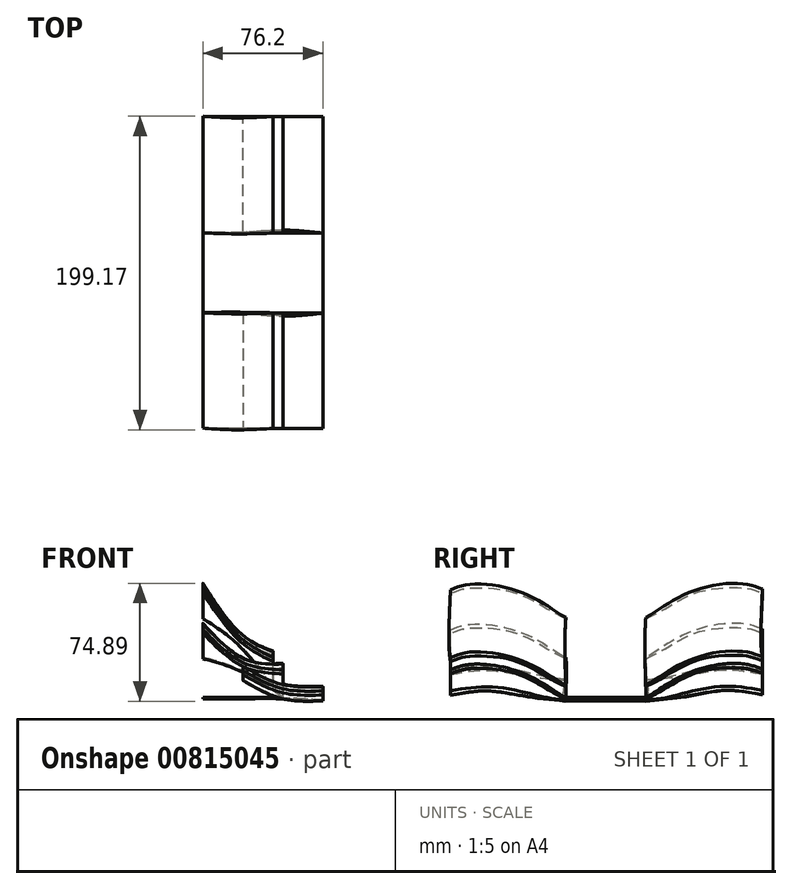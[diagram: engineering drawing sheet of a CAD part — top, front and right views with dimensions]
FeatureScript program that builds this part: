
annotation { "Feature Type Name" : "Feature", "Feature Type Description" : "" }
export const myFeature = defineFeature(function(context is Context, id is Id, definition is map)
    precondition{}
    {
        {
            var Q0;
            Q0=qCreatedBy(makeId("Right.planeOp"),FACE);
            cPlane(context, id + "F0", {"entities" : qUnion([Q0]), "cplaneType" : CPlaneType.OFFSET, "offset" : 25.4 * mm, "width" : 152.4 * mm, "height" : 152.4 * mm});
        }
        {
            var Q0;
            Q0=qCreatedBy(makeId("Right.planeOp"),FACE);
            cPlane(context, id + "F1", {"entities" : qUnion([Q0]), "cplaneType" : CPlaneType.OFFSET, "offset" : 25.4 * mm, "oppositeDirection" : true, "width" : 152.4 * mm, "height" : 152.4 * mm});
        }
        {
            var Q0;
            Q0=qCreatedBy(makeId("Right.planeOp"),FACE);
            cPlane(context, id + "F2", {"entities" : qUnion([Q0]), "cplaneType" : CPlaneType.OFFSET, "offset" : 50.8 * mm, "oppositeDirection" : true, "width" : 152.4 * mm, "height" : 152.4 * mm});
        }
        {
            var Q0;
            Q0=qCreatedBy(makeId("Right.planeOp"),FACE);
            cPlane(context, id + "F3", {"entities" : qUnion([Q0]), "cplaneType" : CPlaneType.OFFSET, "offset" : 6.35 * mm, "oppositeDirection" : true, "width" : 152.4 * mm, "height" : 152.4 * mm});
        }
        {
            var Q0;
            Q0=qCreatedBy(makeId("Right.planeOp"),FACE);
            var sketch = newSketch(context, id + "F4", { "sketchPlane" : qUnion([Q0])});
            skLineSegment(sketch, "E0", {"start": v(-25.85, 6.27) * mm, "end": v(24.95, 6.27) * mm});
            skFitSpline(sketch, "E1", {"points": [v(99.07, 10.46) * mm, v(73.66, 13) * mm, v(48.26, 8.81) * mm, v(24.95, 6.27) * mm], "startDerivative": vector(-112.97, 16.95) * mm, "endDerivative": vector(-94.23, -11.78) * mm});
            skFitSpline(sketch, "E2", {"points": [v(-99.06, 10.06) * mm, v(-73.66, 12.6) * mm, v(-48.26, 8.81) * mm, v(-25.85, 6.27) * mm], "startDerivative": vector(112.13, 16.82) * mm, "endDerivative": vector(95.43, -11.93) * mm});
            skFitSpline(sketch, "E3", {"points": [v(-25.85, 7.04) * mm, v(-45.21, 10.06) * mm, v(-72.39, 15.14) * mm, v(-99.06, 12.6) * mm], "startDerivative": vector(-84.02, 3.38) * mm, "endDerivative": vector(-76.8, -13.35) * mm});
            skFitSpline(sketch, "E4", {"points": [v(24.95, 7.04) * mm, v(45.21, 10.08) * mm, v(72.4, 15.54) * mm, v(99.06, 13) * mm], "startDerivative": vector(91.6, 3.53) * mm, "endDerivative": vector(77.34, -13.44) * mm});
            skLineSegment(sketch, "E5", {"start": v(-25.85, 7.04) * mm, "end": v(24.95, 7.04) * mm});
            skLineSegment(sketch, "E6", {"start": v(-99.06, 12.6) * mm, "end": v(-99.06, 10.06) * mm});
            skLineSegment(sketch, "E7", {"start": v(99.06, 10.46) * mm, "end": v(99.06, 13) * mm});
            skLineSegment(sketch, "E8", {"start": v(-25.85, 7.04) * mm, "end": v(-25.85, 6.27) * mm});
            skLineSegment(sketch, "E9", {"start": v(24.95, 6.27) * mm, "end": v(24.95, 7.04) * mm});
            skFitSpline(sketch, "E10", {"points": [v(-25.85, 6.27) * mm, v(-43.98, 16.13) * mm, v(-63.82, 24.03) * mm, v(-88.57, 25.3) * mm, v(-99.06, 22.13) * mm], "startDerivative": vector(-69.96, 28.98) * mm, "endDerivative": vector(-79.54, -30.53) * mm});
            skLineSegment(sketch, "E11", {"start": v(-99.06, 22.13) * mm, "end": v(-99.06, 24.67) * mm});
            skFitSpline(sketch, "E12", {"points": [v(-99.06, 24.67) * mm, v(-88.75, 27.84) * mm, v(-66.16, 26.57) * mm, v(-42.63, 17.53) * mm, v(-25.85, 7.04) * mm], "startDerivative": vector(50.78, 20.31) * mm, "endDerivative": vector(71.67, -41.09) * mm});
            skFitSpline(sketch, "E13", {"points": [v(24.95, 6.27) * mm, v(43.1, 16.13) * mm, v(62.93, 24.43) * mm, v(88.57, 25.7) * mm, v(99.06, 22.52) * mm], "startDerivative": vector(70.38, 29.15) * mm, "endDerivative": vector(80.02, -30.71) * mm});
            skLineSegment(sketch, "E14", {"start": v(99.06, 22.52) * mm, "end": v(99.06, 25.06) * mm});
            skFitSpline(sketch, "E15", {"points": [v(99.06, 25.06) * mm, v(88.75, 28.24) * mm, v(65.26, 26.97) * mm, v(41.74, 17.53) * mm, v(24.95, 7.04) * mm], "startDerivative": vector(-51.09, 20.43) * mm, "endDerivative": vector(-72.11, -41.34) * mm});
            skSolve(sketch);
        }
        {
            var Q0;
            Q0=qCreatedBy(id+"F1.planeOp",FACE);
            var sketch = newSketch(context, id + "F5", { "sketchPlane" : qUnion([Q0])});
            skFitSpline(sketch, "E16", {"points": [v(99.06, 21.77) * mm, v(73.66, 24.3) * mm, v(48.26, 20.48) * mm, v(25.4, 17.94) * mm], "startDerivative": vector(-112.5, 16.87) * mm, "endDerivative": vector(-94.8, -11.84) * mm});
            skFitSpline(sketch, "E17", {"points": [v(-99.06, 21.76) * mm, v(-73.66, 24.3) * mm, v(-48.26, 20.48) * mm, v(-25.4, 17.94) * mm], "startDerivative": vector(112.48, 16.87) * mm, "endDerivative": vector(94.8, -11.85) * mm});
            skFitSpline(sketch, "E18", {"points": [v(-25.4, 18.7) * mm, v(-45.21, 21.76) * mm, v(-72.39, 26.84) * mm, v(-99.06, 24.3) * mm], "startDerivative": vector(-87.77, 3.58) * mm, "endDerivative": vector(-77.05, -13.4) * mm});
            skFitSpline(sketch, "E19", {"points": [v(25.4, 18.7) * mm, v(45.21, 21.75) * mm, v(72.4, 26.85) * mm, v(99.06, 24.3) * mm], "startDerivative": vector(87.85, 3.55) * mm, "endDerivative": vector(77.06, -13.4) * mm});
            skLineSegment(sketch, "E20", {"start": v(-99.06, 24.3) * mm, "end": v(-99.06, 21.76) * mm});
            skLineSegment(sketch, "E21", {"start": v(99.06, 21.77) * mm, "end": v(99.06, 24.3) * mm});
            skLineSegment(sketch, "E22", {"start": v(-25.4, 18.7) * mm, "end": v(-25.4, 17.94) * mm});
            skLineSegment(sketch, "E23", {"start": v(25.4, 18.7) * mm, "end": v(25.4, 17.94) * mm});
            skFitSpline(sketch, "E24", {"points": [v(99.06, 26.85) * mm, v(73.66, 29.4) * mm, v(48.26, 25.57) * mm, v(25.4, 23.03) * mm], "startDerivative": vector(-112.5, 16.87) * mm, "endDerivative": vector(-94.79, -11.84) * mm});
            skFitSpline(sketch, "E25", {"points": [v(-99.06, 26.85) * mm, v(-73.66, 29.39) * mm, v(-48.26, 25.57) * mm, v(-25.4, 23.03) * mm], "startDerivative": vector(112.48, 16.87) * mm, "endDerivative": vector(94.8, -11.85) * mm});
            skFitSpline(sketch, "E26", {"points": [v(-25.4, 23.8) * mm, v(-45.21, 26.85) * mm, v(-72.4, 31.93) * mm, v(-99.06, 29.39) * mm], "startDerivative": vector(-87.8, 3.58) * mm, "endDerivative": vector(-77.05, -13.4) * mm});
            skFitSpline(sketch, "E27", {"points": [v(25.4, 23.8) * mm, v(45.21, 26.84) * mm, v(72.4, 31.93) * mm, v(99.06, 29.4) * mm], "startDerivative": vector(87.89, 3.55) * mm, "endDerivative": vector(77.06, -13.4) * mm});
            skLineSegment(sketch, "E28", {"start": v(-99.06, 29.39) * mm, "end": v(-99.06, 26.85) * mm});
            skLineSegment(sketch, "E29", {"start": v(99.06, 26.85) * mm, "end": v(99.06, 29.4) * mm});
            skLineSegment(sketch, "E30", {"start": v(-25.4, 23.8) * mm, "end": v(-25.4, 23.03) * mm});
            skLineSegment(sketch, "E31", {"start": v(25.4, 23.8) * mm, "end": v(25.4, 23.03) * mm});
            skLineSegment(sketch, "E32.bottom", {"start": v(-25.4, 7.09) * mm, "end": v(25.4, 7.09) * mm});
            skLineSegment(sketch, "E32.top", {"start": v(-25.4, 6.32) * mm, "end": v(25.4, 6.32) * mm});
            skLineSegment(sketch, "E32.left", {"start": v(-25.4, 7.09) * mm, "end": v(-25.4, 6.32) * mm});
            skLineSegment(sketch, "E32.right", {"start": v(25.4, 7.09) * mm, "end": v(25.4, 6.32) * mm});
            skSolve(sketch);
        }
        {
            var Q0;
            Q0=qCreatedBy(id+"F0.planeOp",FACE);
            var sketch = newSketch(context, id + "F6", { "sketchPlane" : qUnion([Q0])});
            skLineSegment(sketch, "E33", {"start": v(-25.86, 4.98) * mm, "end": v(24.94, 4.98) * mm});
            skFitSpline(sketch, "E34", {"points": [v(99.06, 9.1) * mm, v(73.66, 11.65) * mm, v(48.26, 7.52) * mm, v(24.94, 4.98) * mm], "startDerivative": vector(-112.88, 16.93) * mm, "endDerivative": vector(-94.2, -11.77) * mm});
            skFitSpline(sketch, "E35", {"points": [v(-99.06, 8.76) * mm, v(-73.66, 11.3) * mm, v(-48.26, 7.52) * mm, v(-25.86, 4.98) * mm], "startDerivative": vector(112.12, 16.82) * mm, "endDerivative": vector(95.45, -11.93) * mm});
            skFitSpline(sketch, "E36", {"points": [v(-25.86, 5.74) * mm, v(-45.21, 8.76) * mm, v(-72.4, 13.84) * mm, v(-99.06, 11.3) * mm], "startDerivative": vector(-83.87, 3.27) * mm, "endDerivative": vector(-76.78, -13.34) * mm});
            skFitSpline(sketch, "E37", {"points": [v(24.94, 5.74) * mm, v(45.21, 8.79) * mm, v(72.4, 14.19) * mm, v(99.06, 11.65) * mm], "startDerivative": vector(91.74, 3.53) * mm, "endDerivative": vector(77.34, -13.44) * mm});
            skLineSegment(sketch, "E38", {"start": v(-25.86, 5.74) * mm, "end": v(24.94, 5.74) * mm});
            skLineSegment(sketch, "E39", {"start": v(-99.06, 11.3) * mm, "end": v(-99.06, 8.76) * mm});
            skLineSegment(sketch, "E40", {"start": v(99.06, 9.1) * mm, "end": v(99.06, 11.65) * mm});
            skLineSegment(sketch, "E41", {"start": v(-25.86, 5.74) * mm, "end": v(-25.86, 4.98) * mm});
            skLineSegment(sketch, "E42", {"start": v(24.94, 4.98) * mm, "end": v(24.94, 5.74) * mm});
            skSolve(sketch);
        }
        {
            var Q0;
            Q0=qCreatedBy(id+"F2.planeOp",FACE);
            var sketch = newSketch(context, id + "F7", { "sketchPlane" : qUnion([Q0])});
            skLineSegment(sketch, "E43", {"start": v(-25.76, 32.51) * mm, "end": v(-25.76, 31.75) * mm});
            skLineSegment(sketch, "E44", {"start": v(25.04, 31.75) * mm, "end": v(25.04, 32.51) * mm});
            skFitSpline(sketch, "E45", {"points": [v(-25.76, 31.75) * mm, v(-43.9, 41.6) * mm, v(-63.73, 49.51) * mm, v(-88.49, 50.78) * mm, v(-98.98, 47.6) * mm], "startDerivative": vector(-69.96, 28.98) * mm, "endDerivative": vector(-79.54, -30.53) * mm});
            skLineSegment(sketch, "E46", {"start": v(-98.98, 47.6) * mm, "end": v(-98.98, 50.15) * mm});
            skFitSpline(sketch, "E47", {"points": [v(-98.98, 50.15) * mm, v(-88.66, 53.32) * mm, v(-66.07, 52.05) * mm, v(-42.55, 43) * mm, v(-25.76, 32.51) * mm], "startDerivative": vector(50.78, 20.31) * mm, "endDerivative": vector(71.67, -41.09) * mm});
            skFitSpline(sketch, "E48", {"points": [v(25.04, 31.75) * mm, v(43.17, 41.6) * mm, v(63.01, 49.9) * mm, v(88.65, 51.17) * mm, v(99.14, 48) * mm], "startDerivative": vector(70.38, 29.15) * mm, "endDerivative": vector(80.02, -30.71) * mm});
            skLineSegment(sketch, "E49", {"start": v(99.14, 48) * mm, "end": v(99.14, 50.54) * mm});
            skFitSpline(sketch, "E50", {"points": [v(99.14, 50.54) * mm, v(88.83, 53.71) * mm, v(65.35, 52.44) * mm, v(41.83, 43) * mm, v(25.04, 32.51) * mm], "startDerivative": vector(-51.09, 20.43) * mm, "endDerivative": vector(-72.11, -41.34) * mm});
            skLineSegment(sketch, "E51", {"start": v(-25.73, 57.91) * mm, "end": v(-25.73, 57.15) * mm});
            skLineSegment(sketch, "E52", {"start": v(25.07, 57.15) * mm, "end": v(25.07, 57.91) * mm});
            skFitSpline(sketch, "E53", {"points": [v(-25.73, 57.15) * mm, v(-43.87, 67) * mm, v(-63.7, 74.91) * mm, v(-88.46, 76.18) * mm, v(-98.95, 73) * mm], "startDerivative": vector(-69.96, 28.98) * mm, "endDerivative": vector(-79.54, -30.53) * mm});
            skLineSegment(sketch, "E54", {"start": v(-98.95, 73) * mm, "end": v(-98.95, 75.55) * mm});
            skFitSpline(sketch, "E55", {"points": [v(-98.95, 75.55) * mm, v(-88.64, 78.72) * mm, v(-66.04, 77.45) * mm, v(-42.52, 68.4) * mm, v(-25.73, 57.91) * mm], "startDerivative": vector(50.78, 20.31) * mm, "endDerivative": vector(71.67, -41.09) * mm});
            skFitSpline(sketch, "E56", {"points": [v(25.07, 57.15) * mm, v(43.2, 67) * mm, v(63.04, 75.3) * mm, v(88.68, 76.57) * mm, v(99.17, 73.4) * mm], "startDerivative": vector(70.38, 29.15) * mm, "endDerivative": vector(80.02, -30.71) * mm});
            skLineSegment(sketch, "E57", {"start": v(99.17, 73.4) * mm, "end": v(99.17, 75.94) * mm});
            skFitSpline(sketch, "E58", {"points": [v(99.17, 75.94) * mm, v(88.86, 79.11) * mm, v(65.38, 77.84) * mm, v(41.86, 68.4) * mm, v(25.07, 57.91) * mm], "startDerivative": vector(-51.09, 20.43) * mm, "endDerivative": vector(-72.11, -41.34) * mm});
            skSolve(sketch);
        }
        {
            var Q0;
            Q0=qCreatedBy(id+"F1.planeOp",FACE);
            var sketch = newSketch(context, id + "F8", { "sketchPlane" : qUnion([Q0])});
            skFitSpline(sketch, "E59", {"points": [v(98.14, 41.32) * mm, v(72.74, 43.86) * mm, v(47.34, 40.04) * mm, v(24.48, 37.5) * mm], "startDerivative": vector(-112.5, 16.87) * mm, "endDerivative": vector(-94.79, -11.84) * mm});
            skFitSpline(sketch, "E60", {"points": [v(-99.98, 41.31) * mm, v(-74.58, 43.85) * mm, v(-49.18, 40.04) * mm, v(-26.32, 37.5) * mm], "startDerivative": vector(112.48, 16.87) * mm, "endDerivative": vector(94.8, -11.85) * mm});
            skFitSpline(sketch, "E61", {"points": [v(-26.32, 38.26) * mm, v(-46.13, 41.31) * mm, v(-73.3, 46.4) * mm, v(-99.98, 43.85) * mm], "startDerivative": vector(-87.8, 3.58) * mm, "endDerivative": vector(-77.05, -13.4) * mm});
            skFitSpline(sketch, "E62", {"points": [v(24.48, 38.26) * mm, v(44.3, 41.31) * mm, v(71.47, 46.4) * mm, v(98.14, 43.86) * mm], "startDerivative": vector(87.89, 3.55) * mm, "endDerivative": vector(77.06, -13.4) * mm});
            skLineSegment(sketch, "E63", {"start": v(-99.98, 43.85) * mm, "end": v(-99.98, 41.31) * mm});
            skLineSegment(sketch, "E64", {"start": v(98.14, 41.32) * mm, "end": v(98.14, 43.86) * mm});
            skLineSegment(sketch, "E65", {"start": v(-26.32, 38.26) * mm, "end": v(-26.32, 37.5) * mm});
            skLineSegment(sketch, "E66", {"start": v(24.48, 38.26) * mm, "end": v(24.48, 37.5) * mm});
            skSolve(sketch);
        }
        {
            var Q0;
            Q0=qCreatedBy(id+"F3.planeOp",FACE);
            var sketch = newSketch(context, id + "F9", { "sketchPlane" : qUnion([Q0])});
            skLineSegment(sketch, "E67", {"start": v(-25.84, 14.85) * mm, "end": v(-25.84, 14.09) * mm});
            skLineSegment(sketch, "E68", {"start": v(24.96, 14.09) * mm, "end": v(24.96, 14.85) * mm});
            skFitSpline(sketch, "E69", {"points": [v(-25.84, 14.09) * mm, v(-43.97, 23.94) * mm, v(-63.81, 31.85) * mm, v(-88.56, 33.12) * mm, v(-99.05, 29.94) * mm], "startDerivative": vector(-69.96, 28.98) * mm, "endDerivative": vector(-79.54, -30.53) * mm});
            skLineSegment(sketch, "E70", {"start": v(-99.05, 29.94) * mm, "end": v(-99.05, 32.48) * mm});
            skFitSpline(sketch, "E71", {"points": [v(-99.05, 32.48) * mm, v(-88.74, 35.66) * mm, v(-66.15, 34.39) * mm, v(-42.63, 25.34) * mm, v(-25.84, 14.85) * mm], "startDerivative": vector(50.78, 20.31) * mm, "endDerivative": vector(71.67, -41.09) * mm});
            skFitSpline(sketch, "E72", {"points": [v(24.96, 14.09) * mm, v(43.1, 23.94) * mm, v(62.93, 32.24) * mm, v(88.58, 33.51) * mm, v(99.07, 30.34) * mm], "startDerivative": vector(70.38, 29.15) * mm, "endDerivative": vector(80.02, -30.71) * mm});
            skLineSegment(sketch, "E73", {"start": v(99.07, 30.34) * mm, "end": v(99.07, 32.88) * mm});
            skFitSpline(sketch, "E74", {"points": [v(99.07, 32.88) * mm, v(88.75, 36.05) * mm, v(65.27, 34.78) * mm, v(41.75, 25.34) * mm, v(24.96, 14.85) * mm], "startDerivative": vector(-51.09, 20.43) * mm, "endDerivative": vector(-72.11, -41.34) * mm});
            skSolve(sketch);
        }
        {
            var Q0;
            Q0=qCreatedBy(id+"F2.planeOp",FACE);
            var sketch = newSketch(context, id + "F10", { "sketchPlane" : qUnion([Q0])});
            skLineSegment(sketch, "E75.bottom", {"start": v(-25.4, 7.04) * mm, "end": v(25.4, 7.04) * mm});
            skLineSegment(sketch, "E75.top", {"start": v(-25.4, 6.27) * mm, "end": v(25.4, 6.27) * mm});
            skLineSegment(sketch, "E75.left", {"start": v(-25.4, 7.04) * mm, "end": v(-25.4, 6.27) * mm});
            skLineSegment(sketch, "E75.right", {"start": v(25.4, 7.04) * mm, "end": v(25.4, 6.27) * mm});
            skSolve(sketch);
        }
        {
            var Q0;
            Q0=makeQuery(id+"F5.imprint","IMPRINT",FACE,{"disambiguationData":[TD([[makeQuery(id+"F5.imprint","IMPRINT",EDGE,{"derivedFrom":sQuery(id+"F5.wireOp",EDGE,"E17")}),1.0]])]});
            var Q1;
            {var subQ0=sQuery(id+"F4.wireOp",EDGE,"E2");Q1=makeQuery(id+"F4.imprint","IMPRINT",FACE,{"disambiguationData":[TD([[makeQuery(id+"F4.imprint","IMPRINT",EDGE,{"derivedFrom":subQ0}),1.0]])]});}
            var Q2;
            Q2=makeQuery(id+"F6.imprint","IMPRINT",FACE,{"disambiguationData":[TD([[makeQuery(id+"F6.imprint","IMPRINT",EDGE,{"derivedFrom":sQuery(id+"F6.wireOp",EDGE,"E35")}),1.0]])]});
            loft(context, id + "F11", {"sheetProfilesArray" : [{ "sheetProfileEntities" : qUnion([Q0]) }, { "sheetProfileEntities" : qUnion([Q1]) }, { "sheetProfileEntities" : qUnion([Q2]) }]});
        }
        {
            var Q0;
            Q0=makeQuery(id+"F5.imprint","IMPRINT",FACE,{"disambiguationData":[TD([[makeQuery(id+"F5.imprint","IMPRINT",EDGE,{"derivedFrom":sQuery(id+"F5.wireOp",EDGE,"E16")}),-1.0]])]});
            var Q1;
            {var subQ0=sQuery(id+"F4.wireOp",EDGE,"E1");Q1=makeQuery(id+"F4.imprint","IMPRINT",FACE,{"disambiguationData":[TD([[makeQuery(id+"F4.imprint","IMPRINT",EDGE,{"derivedFrom":subQ0}),-1.0]])]});}
            var Q2;
            Q2=makeQuery(id+"F6.imprint","IMPRINT",FACE,{"disambiguationData":[TD([[makeQuery(id+"F6.imprint","IMPRINT",EDGE,{"derivedFrom":sQuery(id+"F6.wireOp",EDGE,"E34")}),-1.0]])]});
            loft(context, id + "F12", {"sheetProfilesArray" : [{ "sheetProfileEntities" : qUnion([Q0]) }, { "sheetProfileEntities" : qUnion([Q1]) }, { "sheetProfileEntities" : qUnion([Q2]) }]});
        }
        {
            var Q0;
            {var subQ4=sQuery(id+"F4.wireOp",EDGE,"E11");Q0=makeQuery(id+"F4.imprint","IMPRINT",FACE,{"disambiguationData":[TD([[makeQuery(id+"F4.imprint","IMPRINT",EDGE,{"derivedFrom":subQ4}),-1.0]])]});}
            var Q1;
            Q1=makeQuery(id+"F5.imprint","IMPRINT",FACE,{"disambiguationData":[TD([[makeQuery(id+"F5.imprint","IMPRINT",EDGE,{"derivedFrom":sQuery(id+"F5.wireOp",EDGE,"E25")}),1.0]])]});
            var Q2;
            Q2=makeQuery(id+"F7.imprint","IMPRINT",FACE,{"disambiguationData":[TD([[makeQuery(id+"F7.imprint","IMPRINT",EDGE,{"derivedFrom":sQuery(id+"F7.wireOp",EDGE,"E43")}),-1.0]])]});
            loft(context, id + "F13", {"sheetProfilesArray" : [{ "sheetProfileEntities" : qUnion([Q0]) }, { "sheetProfileEntities" : qUnion([Q1]) }, { "sheetProfileEntities" : qUnion([Q2]) }]});
        }
        {
            var Q0;
            {var subQ4=sQuery(id+"F4.wireOp",EDGE,"E14");Q0=makeQuery(id+"F4.imprint","IMPRINT",FACE,{"disambiguationData":[TD([[makeQuery(id+"F4.imprint","IMPRINT",EDGE,{"derivedFrom":subQ4}),1.0]])]});}
            var Q1;
            Q1=makeQuery(id+"F5.imprint","IMPRINT",FACE,{"disambiguationData":[TD([[makeQuery(id+"F5.imprint","IMPRINT",EDGE,{"derivedFrom":sQuery(id+"F5.wireOp",EDGE,"E24")}),-1.0]])]});
            var Q2;
            Q2=makeQuery(id+"F7.imprint","IMPRINT",FACE,{"disambiguationData":[TD([[makeQuery(id+"F7.imprint","IMPRINT",EDGE,{"derivedFrom":sQuery(id+"F7.wireOp",EDGE,"E44")}),-1.0]])]});
            loft(context, id + "F14", {"sheetProfilesArray" : [{ "sheetProfileEntities" : qUnion([Q0]) }, { "sheetProfileEntities" : qUnion([Q1]) }, { "sheetProfileEntities" : qUnion([Q2]) }]});
        }
        {
            var Q0;
            Q0=makeQuery(id+"F7.imprint","IMPRINT",FACE,{"disambiguationData":[TD([[makeQuery(id+"F7.imprint","IMPRINT",EDGE,{"derivedFrom":sQuery(id+"F7.wireOp",EDGE,"E51")}),-1.0]])]});
            var Q1;
            Q1=makeQuery(id+"F8.imprint","IMPRINT",FACE,{"disambiguationData":[TD([[makeQuery(id+"F8.imprint","IMPRINT",EDGE,{"derivedFrom":sQuery(id+"F8.wireOp",EDGE,"E60")}),1.0]])]});
            var Q2;
            Q2=makeQuery(id+"F9.imprint","IMPRINT",FACE,{"disambiguationData":[TD([[makeQuery(id+"F9.imprint","IMPRINT",EDGE,{"derivedFrom":sQuery(id+"F9.wireOp",EDGE,"E67")}),-1.0]])]});
            loft(context, id + "F15", {"sheetProfilesArray" : [{ "sheetProfileEntities" : qUnion([Q0]) }, { "sheetProfileEntities" : qUnion([Q1]) }, { "sheetProfileEntities" : qUnion([Q2]) }]});
        }
        {
            var Q0;
            Q0=makeQuery(id+"F7.imprint","IMPRINT",FACE,{"disambiguationData":[TD([[makeQuery(id+"F7.imprint","IMPRINT",EDGE,{"derivedFrom":sQuery(id+"F7.wireOp",EDGE,"E52")}),-1.0]])]});
            var Q1;
            Q1=makeQuery(id+"F8.imprint","IMPRINT",FACE,{"disambiguationData":[TD([[makeQuery(id+"F8.imprint","IMPRINT",EDGE,{"derivedFrom":sQuery(id+"F8.wireOp",EDGE,"E59")}),-1.0]])]});
            var Q2;
            Q2=makeQuery(id+"F9.imprint","IMPRINT",FACE,{"disambiguationData":[TD([[makeQuery(id+"F9.imprint","IMPRINT",EDGE,{"derivedFrom":sQuery(id+"F9.wireOp",EDGE,"E68")}),-1.0]])]});
            loft(context, id + "F16", {"sheetProfilesArray" : [{ "sheetProfileEntities" : qUnion([Q0]) }, { "sheetProfileEntities" : qUnion([Q1]) }, { "sheetProfileEntities" : qUnion([Q2]) }]});
        }
        {
            var Q0;
            Q0=makeQuery(id+"F10.imprint","IMPRINT",FACE,{"disambiguationData":[TD([[makeQuery(id+"F10.imprint","IMPRINT",EDGE,{"derivedFrom":sQuery(id+"F10.wireOp",EDGE,"E75.bottom")}),-1.0]])]});
            var Q1;
            Q1=makeQuery(id+"F5.imprint","IMPRINT",FACE,{"disambiguationData":[TD([[makeQuery(id+"F5.imprint","IMPRINT",EDGE,{"derivedFrom":sQuery(id+"F5.wireOp",EDGE,"E32.bottom")}),-1.0]])]});
            var Q2;
            Q2=makeQuery(id+"F4.imprint","IMPRINT",FACE,{"disambiguationData":[TD([[makeQuery(id+"F4.imprint","IMPRINT",EDGE,{"derivedFrom":sQuery(id+"F4.wireOp",EDGE,"E0")}),1.0]])]});
            var Q3;
            Q3=makeQuery(id+"F6.imprint","IMPRINT",FACE,{"disambiguationData":[TD([[makeQuery(id+"F6.imprint","IMPRINT",EDGE,{"derivedFrom":sQuery(id+"F6.wireOp",EDGE,"E33")}),1.0]])]});
            loft(context, id + "F17", {"sheetProfilesArray" : [{ "sheetProfileEntities" : qUnion([Q0]) }, { "sheetProfileEntities" : qUnion([Q1]) }, { "sheetProfileEntities" : qUnion([Q2]) }, { "sheetProfileEntities" : qUnion([Q3]) }]});
        }
    });
